# Revit family: QF_MACON_MN7xC-x
name_source: partatom
category: Equipamento especial
units: mm (PartAtom-declared; Revit-internal decimal feet)

## family parameters
Com base no plano de trabalho = Não
Compartilhado = Não
Corte com vazios quando carregada = Não
Cota do conector redondo = Utilizar diâmetro
Número OmniClass = 23.40.40.14.17
Ponto de cálculo do ambiente = Não
Sempre na vertical = Sim
Tipo de parte = Normal
Título OmniClass = Food Cooking Equipment

## types (4) — shared parameters
Depth = 745 mm
Elevação padrão = 0 mm
Fabricante = MACOM
Height = 245 mm
URL = https://www.acosmacom.com.br

## per-type parameters (varying)
| type | Descrição | Door 1 | Door 2 | Show Clearances | Volume | Weight | Width |
| MN72C-G | MÓDULO NEUTRO COM GAVETA 720 MACOM | Sim | Sim | Sim | 1,3 m³ | 20,00 kg | 720 mm |
| MN71C-G | MÓDULO NEUTRO COM GAVETA 360 MACOM | Sim | Sim | Sim | 0,06 m³ | 13,00 kg | 360 mm |
| MN72C-S | MÓDULO NEUTRO SIMPLES 720 MACOM | Não | Não | Não | 1,3 m³ | 20,00 kg | 720 mm |
| MN71C-S | MÓDULO NEUTRO SIMPLES 360 MACOM | Não | Não | Não | 0,06 m³ | 13,00 kg | 360 mm |

note: column(s) folded — value = type name in every type: Modelo
